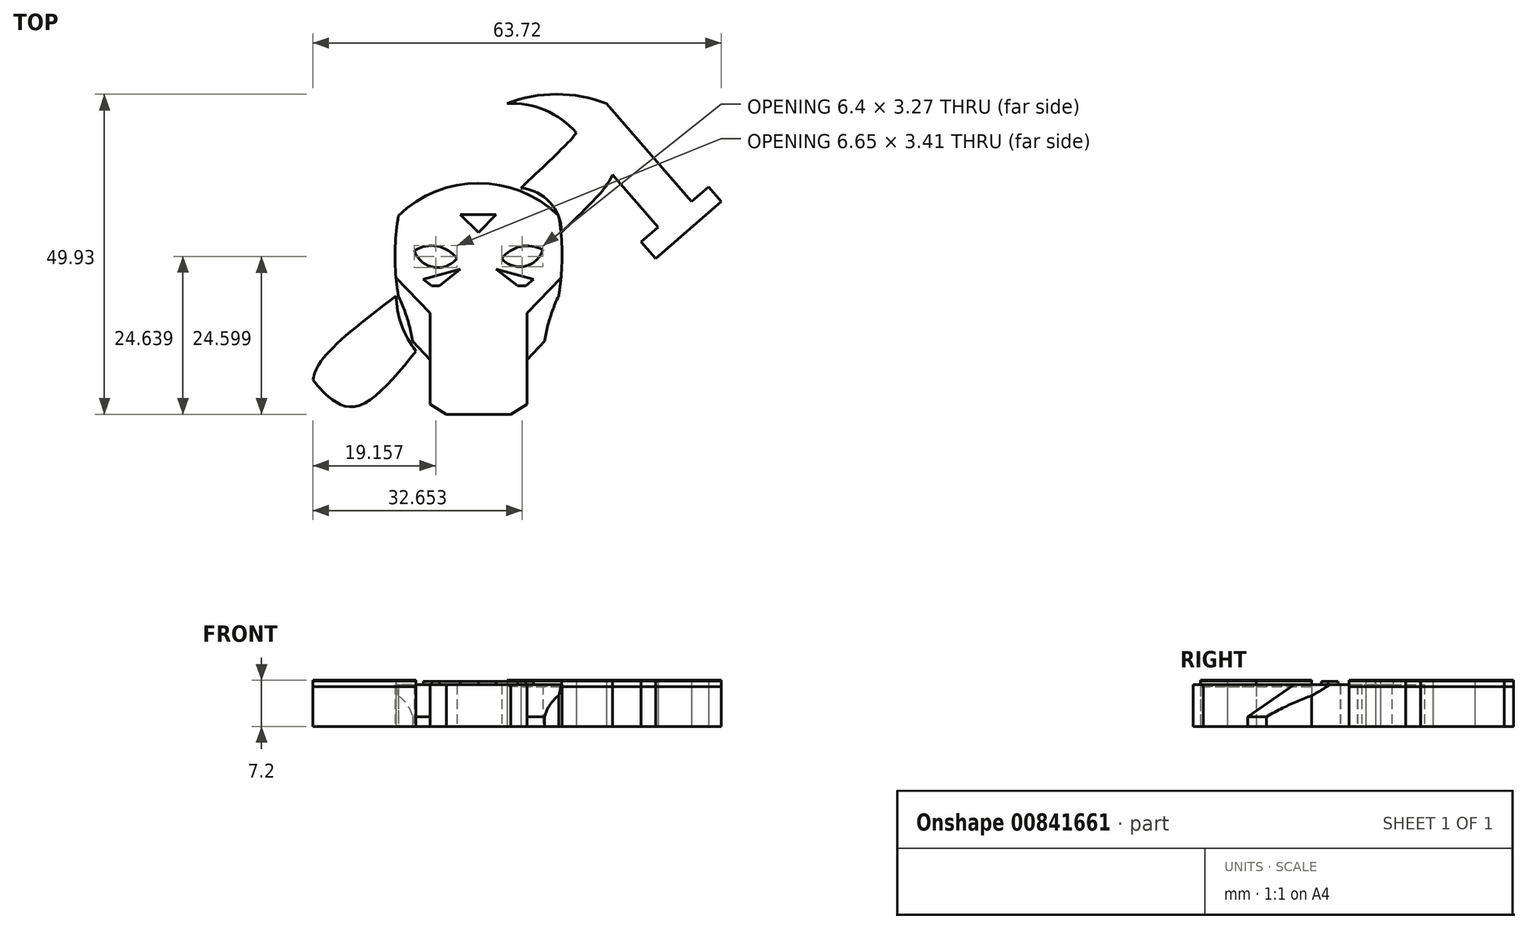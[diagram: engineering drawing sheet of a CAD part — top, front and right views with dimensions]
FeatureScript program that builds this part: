
annotation { "Feature Type Name" : "Feature", "Feature Type Description" : "" }
export const myFeature = defineFeature(function(context is Context, id is Id, definition is map)
    precondition{}
    {
        {
            var Q0;
            Q0=qCreatedBy(makeId("Top.planeOp"),FACE);
            var sketch = newSketch(context, id + "F0", { "sketchPlane" : qUnion([Q0])});
            skLineSegment(sketch, "E0.bottom", {"start": v(0, -18.48) * mm, "end": v(-5, -18.48) * mm});
            skLineSegment(sketch, "E1.top", {"start": v(0, -18.48) * mm, "end": v(5, -18.48) * mm});
            skLineSegment(sketch, "E2", {"start": v(-5, -18.48) * mm, "end": v(-7.55, -16.9) * mm});
            skLineSegment(sketch, "E3", {"start": v(-7.55, -16.9) * mm, "end": v(-7.55, -9.96) * mm});
            skLineSegment(sketch, "E4", {"start": v(5, -18.48) * mm, "end": v(7.55, -16.9) * mm});
            skLineSegment(sketch, "E5", {"start": v(7.55, -16.9) * mm, "end": v(7.55, -9.96) * mm});
            skLineSegment(sketch, "E6", {"start": v(-7.55, -9.96) * mm, "end": v(-10.3, -7.07) * mm});
            skLineSegment(sketch, "E7", {"start": v(7.55, -9.96) * mm, "end": v(10.3, -7.07) * mm});
            skArc(sketch, "E8", {"start": v(-10.3, -7.07) * mm, "mid": v(-11.14, -3.45) * mm, "end": v(-12.5, 0) * mm});
            skArc(sketch, "E9", {"start": v(12.5, 0) * mm, "mid": v(11.14, -3.45) * mm, "end": v(10.3, -7.07) * mm});
            skPoint(sketch, "E10", {"position": v(0, 12.5) * mm});
            skArc(sketch, "E11", {"start": v(-12.5, 12.5) * mm, "mid": v(-13.02, 6.25) * mm, "end": v(-12.5, 0) * mm});
            skArc(sketch, "E12", {"start": v(12.5, 0) * mm, "mid": v(13.02, 6.25) * mm, "end": v(12.5, 12.5) * mm});
            skArc(sketch, "E13", {"start": v(12.5, 12.5) * mm, "mid": v(0, 17.56) * mm, "end": v(-12.5, 12.5) * mm});
            skArc(sketch, "E14", {"start": v(-3.36, 5.8) * mm, "mid": v(-6.44, 7.73) * mm, "end": v(-10, 7.07) * mm});
            skLineSegment(sketch, "E15", {"start": v(-10, 7.07) * mm, "end": v(-13, 7.07) * mm});
            skLineSegment(sketch, "E16", {"start": v(13, 7.07) * mm, "end": v(10.01, 7.18) * mm});
            skArc(sketch, "E17", {"start": v(10.01, 7.18) * mm, "mid": v(6.56, 7.68) * mm, "end": v(3.62, 5.8) * mm});
            skLineSegment(sketch, "E18", {"start": v(3.62, 5.8) * mm, "end": v(-3.36, 5.8) * mm});
            skArc(sketch, "E19", {"start": v(-10, 7.07) * mm, "mid": v(-7.06, 4.47) * mm, "end": v(-3.36, 5.8) * mm});
            skArc(sketch, "E20", {"start": v(3.62, 5.8) * mm, "mid": v(7.22, 4.6) * mm, "end": v(10.01, 7.18) * mm});
            skSolve(sketch);
        }
        {
            var Q0;
            Q0 = qSketchRegion(id + "F0", true);
            extrude(context, id + "F1", {"entities" : qUnion([Q0]), "depth" : 6.5 * mm, "offsetDistance" : 25 * mm});
        }
        {
            var Q0;
            Q0=qCreatedBy(makeId("Top.planeOp"),FACE);
            var sketch = newSketch(context, id + "F2", { "sketchPlane" : qUnion([Q0])});
            skLineSegment(sketch, "E21", {"start": v(0, 12.7) * mm, "end": v(-2.83, 12.7) * mm});
            skLineSegment(sketch, "E22", {"start": v(-2.83, 12.7) * mm, "end": v(0, 9.9) * mm});
            skLineSegment(sketch, "E23", {"start": v(0, 9.9) * mm, "end": v(2.76, 12.7) * mm});
            skLineSegment(sketch, "E24", {"start": v(2.76, 12.7) * mm, "end": v(0, 12.7) * mm});
            skLineSegment(sketch, "E25", {"start": v(-2.83, 4.14) * mm, "end": v(-8.63, 2.59) * mm});
            skLineSegment(sketch, "E26", {"start": v(2.76, 4.14) * mm, "end": v(8.56, 2.59) * mm});
            skLineSegment(sketch, "E27", {"start": v(-2.83, 4.14) * mm, "end": v(-7.33, 1.54) * mm});
            skLineSegment(sketch, "E28", {"start": v(-7.33, 1.54) * mm, "end": v(-8.63, 2.59) * mm});
            skLineSegment(sketch, "E29", {"start": v(2.76, 4.14) * mm, "end": v(7.35, 1.54) * mm});
            skLineSegment(sketch, "E30", {"start": v(7.35, 1.54) * mm, "end": v(8.56, 2.59) * mm});
            skLineSegment(sketch, "E31", {"start": v(-2.83, 4.14) * mm, "end": v(-6.08, 1.54) * mm});
            skLineSegment(sketch, "E32", {"start": v(-6.08, 1.54) * mm, "end": v(-7.33, 1.54) * mm});
            skLineSegment(sketch, "E33", {"start": v(2.76, 4.14) * mm, "end": v(6.1, 1.54) * mm});
            skLineSegment(sketch, "E34", {"start": v(6.1, 1.54) * mm, "end": v(7.35, 1.54) * mm});
            skSolve(sketch);
        }
        {
            var Q0;
            Q0=makeQuery(id+"F1.opExtrude","CAP_EDGE",EDGE,{"disambiguationData":[OSD([sQuery(id+"F0.wireOp",EDGE,"E6")])],"isStart":false});
            var Q1;
            Q1=makeQuery(id+"F1.opExtrude","CAP_EDGE",EDGE,{"disambiguationData":[OSD([sQuery(id+"F0.wireOp",EDGE,"E7")])],"isStart":false});
            chamfer(context, id + "F3", {"entities" : qUnion([Q0, Q1]), "width" : 5 * mm, "tangentPropagation" : true});
        }
        {
            var Q0;
            Q0 = qSketchRegion(id + "F2", true);
            extrude(context, id + "F4", {"entities" : qUnion([Q0]), "operationType" : NewBodyOperationType.ADD, "depth" : 7 * mm, "offsetDistance" : 25 * mm});
        }
        {
            var Q0;
            Q0=qCreatedBy(makeId("Top.planeOp"),FACE);
            var sketch = newSketch(context, id + "F5", { "sketchPlane" : qUnion([Q0])});
            skFitSpline(sketch, "E35", {"points": [v(-25.84, -13.14) * mm, v(-23.59, -15.56) * mm, v(-19.26, -17.3) * mm, v(-9.74, -8.64) * mm], "startDerivative": vector(8.18, -9.94) * mm, "endDerivative": vector(21.17, 25.89) * mm});
            skFitSpline(sketch, "E36", {"points": [v(-25.84, -13.14) * mm, v(-24.45, -10.02) * mm, v(-12.86, 0) * mm], "startDerivative": vector(2.28, 8.91) * mm, "endDerivative": vector(21.4, 16.46) * mm});
            skFitSpline(sketch, "E37", {"points": [v(6.63, 16.81) * mm, v(14.55, 24.55) * mm, v(15.25, 25.43) * mm], "startDerivative": vector(13.29, 12.7) * mm, "endDerivative": vector(2, 2.84) * mm});
            skFitSpline(sketch, "E38", {"points": [v(12.96, 9.95) * mm, v(19.65, 16.81) * mm, v(20.9, 18.91) * mm], "startDerivative": vector(12.16, 11.68) * mm, "endDerivative": vector(2.7, 5.57) * mm});
            skLineSegment(sketch, "E39", {"start": v(15.25, 25.43) * mm, "end": v(28, 10.7) * mm});
            skLineSegment(sketch, "E40", {"start": v(28, 10.7) * mm, "end": v(25.37, 8.41) * mm});
            skLineSegment(sketch, "E41", {"start": v(25.37, 8.41) * mm, "end": v(27.63, 5.8) * mm});
            skLineSegment(sketch, "E42", {"start": v(27.63, 5.8) * mm, "end": v(37.88, 14.68) * mm});
            skLineSegment(sketch, "E43", {"start": v(37.88, 14.68) * mm, "end": v(35.87, 17) * mm});
            skLineSegment(sketch, "E44", {"start": v(35.87, 17) * mm, "end": v(33.2, 14.68) * mm});
            skLineSegment(sketch, "E45", {"start": v(33.2, 14.68) * mm, "end": v(19.93, 30) * mm});
            skArc(sketch, "E46", {"start": v(19.93, 30) * mm, "mid": v(12.17, 31.45) * mm, "end": v(4.42, 30) * mm});
            skArc(sketch, "E47", {"start": v(15.25, 25.43) * mm, "mid": v(10.37, 28.97) * mm, "end": v(4.42, 30) * mm});
            skArc(sketch, "E48", {"start": v(12.96, 9.95) * mm, "mid": v(10.57, 15.05) * mm, "end": v(5.2, 16.72) * mm});
            skArc(sketch, "E49", {"start": v(-12.86, 0) * mm, "mid": v(-12.01, -4.58) * mm, "end": v(-9.74, -8.64) * mm});
            skLineSegment(sketch, "E50", {"start": v(15.25, 25.43) * mm, "end": v(20.9, 18.91) * mm});
            skArc(sketch, "E51", {"start": v(12.96, 9.95) * mm, "mid": v(11.12, 14.6) * mm, "end": v(6.63, 16.81) * mm});
            skSolve(sketch);
        }
        {
            var Q0;
            Q0 = qSketchRegion(id + "F5", true);
            extrude(context, id + "F6", {"entities" : qUnion([Q0]), "depth" : 7.2 * mm, "offsetDistance" : 25 * mm});
        }
        {
            var Q0;
            Q0 = qSketchRegion(id + "F5", true);
            extrude(context, id + "F7", {"entities" : qUnion([Q0]), "depth" : 7.1 * mm, "offsetDistance" : 25 * mm});
        }
        {
            var Q0;
            Q0 = qSketchRegion(id + "F5", true);
            extrude(context, id + "F8", {"entities" : qUnion([Q0]), "depth" : 6.2 * mm, "offsetDistance" : 25 * mm});
        }
    });
